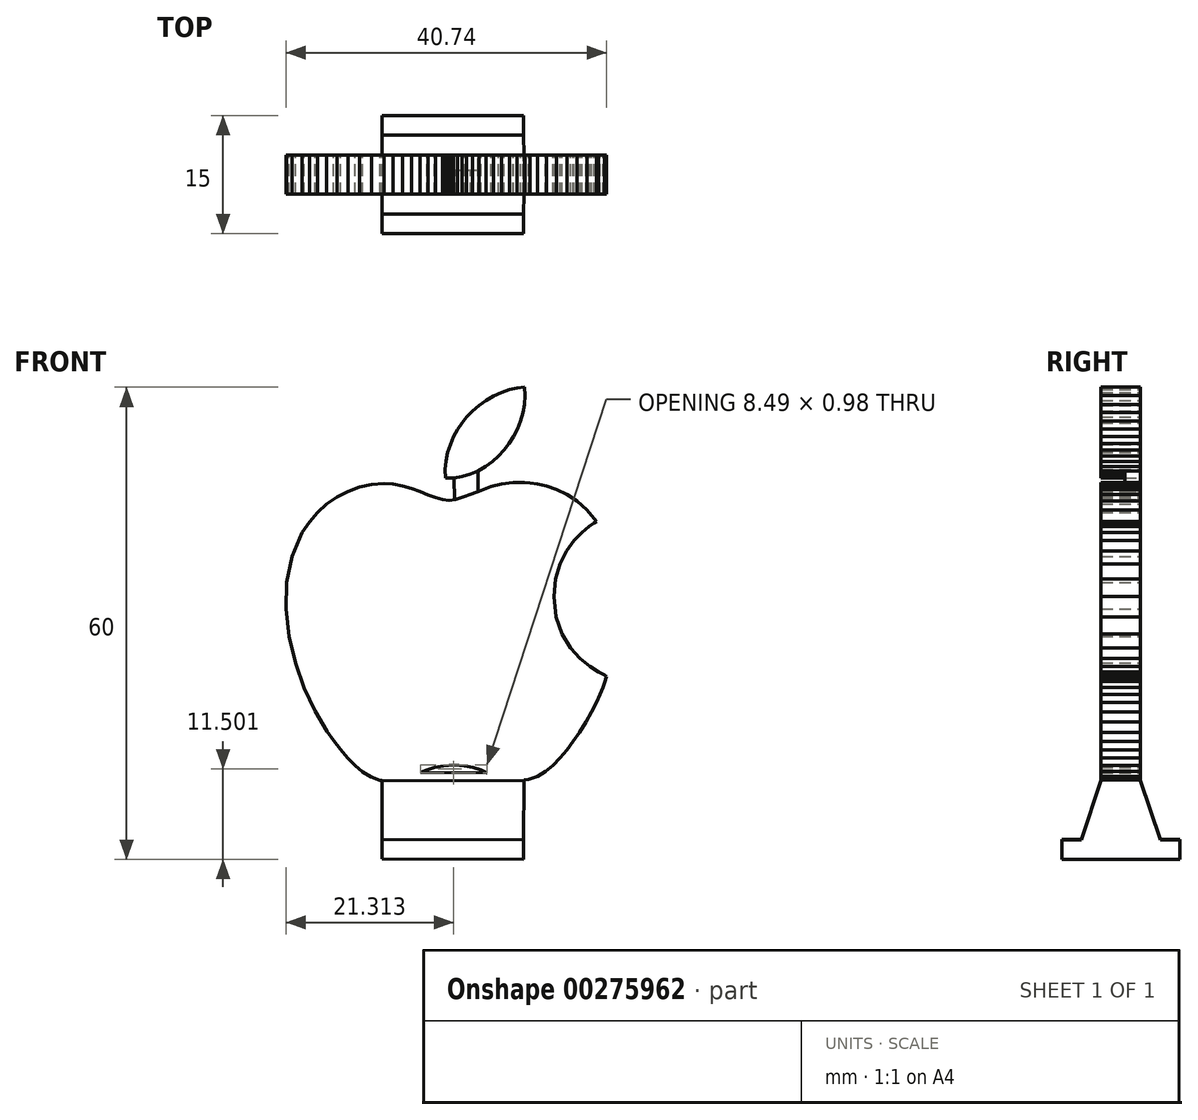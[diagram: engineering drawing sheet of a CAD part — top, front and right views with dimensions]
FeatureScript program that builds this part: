
annotation { "Feature Type Name" : "Feature", "Feature Type Description" : "" }
export const myFeature = defineFeature(function(context is Context, id is Id, definition is map)
    precondition{}
    {
        {
            var Q0;
            Q0=qCreatedBy(makeId("Front.planeOp"),FACE);
            var sketch = newSketch(context, id + "F0", { "sketchPlane" : qUnion([Q0])});
            skLineSegment(sketch, "E0", {"start": v(13.65, -1.57) * mm, "end": v(13.96, -4.18) * mm});
            skLineSegment(sketch, "E1", {"start": v(13.96, -4.18) * mm, "end": v(14.72, -6.34) * mm});
            skLineSegment(sketch, "E2", {"start": v(14.72, -6.34) * mm, "end": v(15.79, -8.1) * mm});
            skLineSegment(sketch, "E3", {"start": v(15.79, -8.1) * mm, "end": v(17, -9.46) * mm});
            skLineSegment(sketch, "E4", {"start": v(17, -9.46) * mm, "end": v(18.23, -10.48) * mm});
            skLineSegment(sketch, "E5", {"start": v(18.23, -10.48) * mm, "end": v(19.3, -11.17) * mm});
            skLineSegment(sketch, "E6", {"start": v(19.3, -11.17) * mm, "end": v(20.06, -11.56) * mm});
            skLineSegment(sketch, "E7", {"start": v(20.06, -11.56) * mm, "end": v(20.37, -11.7) * mm});
            skLineSegment(sketch, "E8", {"start": v(20.37, -11.7) * mm, "end": v(20.3, -11.9) * mm});
            skLineSegment(sketch, "E9", {"start": v(20.3, -11.9) * mm, "end": v(20.14, -12.39) * mm});
            skLineSegment(sketch, "E10", {"start": v(20.14, -12.39) * mm, "end": v(19.89, -13.1) * mm});
            skLineSegment(sketch, "E11", {"start": v(19.89, -13.1) * mm, "end": v(19.52, -14) * mm});
            skLineSegment(sketch, "E12", {"start": v(19.52, -14) * mm, "end": v(19.05, -15.06) * mm});
            skLineSegment(sketch, "E13", {"start": v(19.05, -15.06) * mm, "end": v(18.46, -16.24) * mm});
            skLineSegment(sketch, "E14", {"start": v(18.46, -16.24) * mm, "end": v(17.75, -17.5) * mm});
            skLineSegment(sketch, "E15", {"start": v(17.75, -17.5) * mm, "end": v(16.9, -18.82) * mm});
            skLineSegment(sketch, "E16", {"start": v(16.9, -18.82) * mm, "end": v(16.12, -19.95) * mm});
            skLineSegment(sketch, "E17", {"start": v(16.12, -19.95) * mm, "end": v(15.3, -21.06) * mm});
            skLineSegment(sketch, "E18", {"start": v(15.3, -21.06) * mm, "end": v(14.46, -22.09) * mm});
            skLineSegment(sketch, "E19", {"start": v(14.46, -22.09) * mm, "end": v(13.57, -23.01) * mm});
            skLineSegment(sketch, "E20", {"start": v(13.57, -23.01) * mm, "end": v(12.62, -23.8) * mm});
            skLineSegment(sketch, "E21", {"start": v(12.62, -23.8) * mm, "end": v(11.58, -24.41) * mm});
            skLineSegment(sketch, "E22", {"start": v(11.58, -24.41) * mm, "end": v(10.46, -24.81) * mm});
            skLineSegment(sketch, "E23", {"start": v(10.46, -24.81) * mm, "end": v(9.24, -24.97) * mm});
            skLineSegment(sketch, "E24", {"start": v(9.24, -24.97) * mm, "end": v(8.08, -24.9) * mm});
            skLineSegment(sketch, "E25", {"start": v(8.08, -24.9) * mm, "end": v(7.08, -24.68) * mm});
            skLineSegment(sketch, "E26", {"start": v(7.08, -24.68) * mm, "end": v(6.16, -24.37) * mm});
            skLineSegment(sketch, "E27", {"start": v(6.16, -24.37) * mm, "end": v(5.3, -24) * mm});
            skLineSegment(sketch, "E28", {"start": v(5.3, -24) * mm, "end": v(4.4, -23.63) * mm});
            skLineSegment(sketch, "E29", {"start": v(4.4, -23.63) * mm, "end": v(3.42, -23.3) * mm});
            skLineSegment(sketch, "E30", {"start": v(3.42, -23.3) * mm, "end": v(2.3, -23.07) * mm});
            skLineSegment(sketch, "E31", {"start": v(2.3, -23.07) * mm, "end": v(0.98, -22.98) * mm});
            skLineSegment(sketch, "E32", {"start": v(0.98, -22.98) * mm, "end": v(-0.34, -23.06) * mm});
            skLineSegment(sketch, "E33", {"start": v(-0.34, -23.06) * mm, "end": v(-1.47, -23.28) * mm});
            skLineSegment(sketch, "E34", {"start": v(-1.47, -23.28) * mm, "end": v(-2.46, -23.6) * mm});
            skLineSegment(sketch, "E35", {"start": v(-2.46, -23.6) * mm, "end": v(-3.37, -23.96) * mm});
            skLineSegment(sketch, "E36", {"start": v(-3.37, -23.96) * mm, "end": v(-4.24, -24.33) * mm});
            skLineSegment(sketch, "E37", {"start": v(-4.24, -24.33) * mm, "end": v(-5.14, -24.66) * mm});
            skLineSegment(sketch, "E38", {"start": v(-5.14, -24.66) * mm, "end": v(-6.12, -24.9) * mm});
            skLineSegment(sketch, "E39", {"start": v(-6.12, -24.9) * mm, "end": v(-7.22, -25.03) * mm});
            skLineSegment(sketch, "E40", {"start": v(-7.22, -25.03) * mm, "end": v(-8.42, -24.92) * mm});
            skLineSegment(sketch, "E41", {"start": v(-8.42, -24.92) * mm, "end": v(-9.55, -24.52) * mm});
            skLineSegment(sketch, "E42", {"start": v(-9.55, -24.52) * mm, "end": v(-10.62, -23.88) * mm});
            skLineSegment(sketch, "E43", {"start": v(-10.62, -23.88) * mm, "end": v(-11.62, -23.05) * mm});
            skLineSegment(sketch, "E44", {"start": v(-11.62, -23.05) * mm, "end": v(-12.57, -22.07) * mm});
            skLineSegment(sketch, "E45", {"start": v(-12.57, -22.07) * mm, "end": v(-13.47, -20.98) * mm});
            skLineSegment(sketch, "E46", {"start": v(-13.47, -20.98) * mm, "end": v(-14.32, -19.84) * mm});
            skLineSegment(sketch, "E47", {"start": v(-14.32, -19.84) * mm, "end": v(-15.13, -18.7) * mm});
            skLineSegment(sketch, "E48", {"start": v(-15.13, -18.7) * mm, "end": v(-16.68, -16.14) * mm});
            skLineSegment(sketch, "E49", {"start": v(-16.68, -16.14) * mm, "end": v(-18.06, -13.2) * mm});
            skLineSegment(sketch, "E50", {"start": v(-18.06, -13.2) * mm, "end": v(-19.19, -10) * mm});
            skLineSegment(sketch, "E51", {"start": v(-19.19, -10) * mm, "end": v(-19.98, -6.62) * mm});
            skLineSegment(sketch, "E52", {"start": v(-19.98, -6.62) * mm, "end": v(-20.37, -3.18) * mm});
            skLineSegment(sketch, "E53", {"start": v(-20.37, -3.18) * mm, "end": v(-20.27, 0.23) * mm});
            skLineSegment(sketch, "E54", {"start": v(-20.27, 0.23) * mm, "end": v(-19.6, 3.5) * mm});
            skLineSegment(sketch, "E55", {"start": v(-19.6, 3.5) * mm, "end": v(-18.3, 6.53) * mm});
            skLineSegment(sketch, "E56", {"start": v(-18.3, 6.53) * mm, "end": v(-17.4, 7.89) * mm});
            skLineSegment(sketch, "E57", {"start": v(-17.4, 7.89) * mm, "end": v(-16.36, 9.1) * mm});
            skLineSegment(sketch, "E58", {"start": v(-16.36, 9.1) * mm, "end": v(-15.18, 10.17) * mm});
            skLineSegment(sketch, "E59", {"start": v(-15.18, 10.17) * mm, "end": v(-13.9, 11.07) * mm});
            skLineSegment(sketch, "E60", {"start": v(-13.9, 11.07) * mm, "end": v(-12.51, 11.8) * mm});
            skLineSegment(sketch, "E61", {"start": v(-12.51, 11.8) * mm, "end": v(-11.05, 12.33) * mm});
            skLineSegment(sketch, "E62", {"start": v(-11.05, 12.33) * mm, "end": v(-9.52, 12.67) * mm});
            skLineSegment(sketch, "E63", {"start": v(-9.52, 12.67) * mm, "end": v(-7.94, 12.8) * mm});
            skLineSegment(sketch, "E64", {"start": v(-7.94, 12.8) * mm, "end": v(-6.74, 12.73) * mm});
            skLineSegment(sketch, "E65", {"start": v(-6.74, 12.73) * mm, "end": v(-5.57, 12.5) * mm});
            skLineSegment(sketch, "E66", {"start": v(-5.57, 12.5) * mm, "end": v(-4.43, 12.14) * mm});
            skLineSegment(sketch, "E67", {"start": v(-4.43, 12.14) * mm, "end": v(-3.34, 11.74) * mm});
            skLineSegment(sketch, "E68", {"start": v(-3.34, 11.74) * mm, "end": v(-2.31, 11.33) * mm});
            skLineSegment(sketch, "E69", {"start": v(-2.31, 11.33) * mm, "end": v(-1.35, 10.98) * mm});
            skLineSegment(sketch, "E70", {"start": v(-1.35, 10.98) * mm, "end": v(-0.47, 10.73) * mm});
            skLineSegment(sketch, "E71", {"start": v(-0.47, 10.73) * mm, "end": v(0.32, 10.63) * mm});
            skLineSegment(sketch, "E72", {"start": v(0.32, 10.63) * mm, "end": v(1.14, 10.74) * mm});
            skLineSegment(sketch, "E73", {"start": v(1.14, 10.74) * mm, "end": v(2.1, 11.04) * mm});
            skLineSegment(sketch, "E74", {"start": v(2.1, 11.04) * mm, "end": v(3.2, 11.46) * mm});
            skLineSegment(sketch, "E75", {"start": v(3.2, 11.46) * mm, "end": v(4.4, 11.93) * mm});
            skLineSegment(sketch, "E76", {"start": v(4.4, 11.93) * mm, "end": v(5.68, 12.37) * mm});
            skLineSegment(sketch, "E77", {"start": v(5.68, 12.37) * mm, "end": v(7.04, 12.73) * mm});
            skLineSegment(sketch, "E78", {"start": v(7.04, 12.73) * mm, "end": v(8.45, 12.94) * mm});
            skLineSegment(sketch, "E79", {"start": v(8.45, 12.94) * mm, "end": v(9.9, 12.93) * mm});
            skLineSegment(sketch, "E80", {"start": v(9.9, 12.93) * mm, "end": v(10.65, 12.87) * mm});
            skLineSegment(sketch, "E81", {"start": v(10.65, 12.87) * mm, "end": v(11.6, 12.73) * mm});
            skLineSegment(sketch, "E82", {"start": v(11.6, 12.73) * mm, "end": v(12.74, 12.46) * mm});
            skLineSegment(sketch, "E83", {"start": v(12.74, 12.46) * mm, "end": v(14, 12.03) * mm});
            skLineSegment(sketch, "E84", {"start": v(14, 12.03) * mm, "end": v(15.3, 11.4) * mm});
            skLineSegment(sketch, "E85", {"start": v(15.3, 11.4) * mm, "end": v(16.62, 10.54) * mm});
            skLineSegment(sketch, "E86", {"start": v(16.62, 10.54) * mm, "end": v(17.89, 9.4) * mm});
            skLineSegment(sketch, "E87", {"start": v(17.89, 9.4) * mm, "end": v(19.06, 7.96) * mm});
            skLineSegment(sketch, "E88", {"start": v(19.06, 7.96) * mm, "end": v(18.76, 7.77) * mm});
            skLineSegment(sketch, "E89", {"start": v(18.76, 7.77) * mm, "end": v(18.1, 7.3) * mm});
            skLineSegment(sketch, "E90", {"start": v(18.1, 7.3) * mm, "end": v(17.23, 6.55) * mm});
            skLineSegment(sketch, "E91", {"start": v(17.23, 6.55) * mm, "end": v(16.25, 5.52) * mm});
            skLineSegment(sketch, "E92", {"start": v(16.25, 5.52) * mm, "end": v(15.27, 4.2) * mm});
            skLineSegment(sketch, "E93", {"start": v(15.27, 4.2) * mm, "end": v(14.44, 2.57) * mm});
            skLineSegment(sketch, "E94", {"start": v(14.44, 2.57) * mm, "end": v(13.86, 0.65) * mm});
            skLineSegment(sketch, "E95", {"start": v(13.86, 0.65) * mm, "end": v(13.65, -1.57) * mm});
            skLineSegment(sketch, "E96", {"start": v(7.35, 17.04) * mm, "end": v(7.98, 17.87) * mm});
            skLineSegment(sketch, "E97", {"start": v(7.98, 17.87) * mm, "end": v(8.54, 18.77) * mm});
            skLineSegment(sketch, "E98", {"start": v(8.54, 18.77) * mm, "end": v(9.03, 19.72) * mm});
            skLineSegment(sketch, "E99", {"start": v(9.03, 19.72) * mm, "end": v(9.43, 20.73) * mm});
            skLineSegment(sketch, "E100", {"start": v(9.43, 20.73) * mm, "end": v(9.73, 21.77) * mm});
            skLineSegment(sketch, "E101", {"start": v(9.73, 21.77) * mm, "end": v(9.93, 22.84) * mm});
            skLineSegment(sketch, "E102", {"start": v(9.93, 22.84) * mm, "end": v(10, 23.93) * mm});
            skLineSegment(sketch, "E103", {"start": v(10, 23.93) * mm, "end": v(9.95, 25.03) * mm});
            skLineSegment(sketch, "E104", {"start": v(9.95, 25.03) * mm, "end": v(8.99, 24.93) * mm});
            skLineSegment(sketch, "E105", {"start": v(8.99, 24.93) * mm, "end": v(8, 24.7) * mm});
            skLineSegment(sketch, "E106", {"start": v(8, 24.7) * mm, "end": v(7, 24.34) * mm});
            skLineSegment(sketch, "E107", {"start": v(7, 24.34) * mm, "end": v(6, 23.89) * mm});
            skLineSegment(sketch, "E108", {"start": v(6, 23.89) * mm, "end": v(5.04, 23.34) * mm});
            skLineSegment(sketch, "E109", {"start": v(5.04, 23.34) * mm, "end": v(4.14, 22.7) * mm});
            skLineSegment(sketch, "E110", {"start": v(4.14, 22.7) * mm, "end": v(3.31, 22) * mm});
            skLineSegment(sketch, "E111", {"start": v(3.31, 22) * mm, "end": v(2.58, 21.24) * mm});
            skLineSegment(sketch, "E112", {"start": v(2.58, 21.24) * mm, "end": v(1.98, 20.48) * mm});
            skLineSegment(sketch, "E113", {"start": v(1.98, 20.48) * mm, "end": v(1.43, 19.64) * mm});
            skLineSegment(sketch, "E114", {"start": v(1.43, 19.64) * mm, "end": v(0.93, 18.72) * mm});
            skLineSegment(sketch, "E115", {"start": v(0.93, 18.72) * mm, "end": v(0.5, 17.74) * mm});
            skLineSegment(sketch, "E116", {"start": v(0.5, 17.74) * mm, "end": v(0.17, 16.71) * mm});
            skLineSegment(sketch, "E117", {"start": v(0.17, 16.71) * mm, "end": v(-0.05, 15.65) * mm});
            skLineSegment(sketch, "E118", {"start": v(-0.05, 15.65) * mm, "end": v(-0.14, 14.57) * mm});
            skLineSegment(sketch, "E119", {"start": v(-0.14, 14.57) * mm, "end": v(-0.08, 13.5) * mm});
            skLineSegment(sketch, "E120", {"start": v(-0.08, 13.5) * mm, "end": v(0.98, 13.5) * mm});
            skLineSegment(sketch, "E121", {"start": v(0.98, 13.5) * mm, "end": v(2.02, 13.66) * mm});
            skLineSegment(sketch, "E122", {"start": v(2.02, 13.66) * mm, "end": v(3.05, 13.96) * mm});
            skLineSegment(sketch, "E123", {"start": v(3.05, 13.96) * mm, "end": v(4.03, 14.39) * mm});
            skLineSegment(sketch, "E124", {"start": v(4.03, 14.39) * mm, "end": v(4.97, 14.93) * mm});
            skLineSegment(sketch, "E125", {"start": v(4.97, 14.93) * mm, "end": v(5.85, 15.56) * mm});
            skLineSegment(sketch, "E126", {"start": v(5.85, 15.56) * mm, "end": v(6.64, 16.27) * mm});
            skLineSegment(sketch, "E127", {"start": v(6.64, 16.27) * mm, "end": v(7.35, 17.04) * mm});
            skLineSegment(sketch, "E128", {"start": v(0.98, 13.5) * mm, "end": v(1.14, 8.27) * mm});
            skLineSegment(sketch, "E129", {"start": v(4.03, 14.39) * mm, "end": v(4.03, 8.79) * mm});
            skLineSegment(sketch, "E130", {"start": v(-8.42, -24.92) * mm, "end": v(9.85, -24.97) * mm});
            skPoint(sketch, "E130.endSnap0", {"position": v(9.85, -24.9) * mm});
            skLineSegment(sketch, "E131", {"start": v(0.72, -24.94) * mm, "end": v(0.7, -28.27) * mm});
            skSolve(sketch);
        }
        {
            var Q0;
            Q0=makeQuery(id+"F0.imprint","IMPRINT",FACE,{"disambiguationData":[TD([[makeQuery(id+"F0.imprint","IMPRINT",EDGE,{"derivedFrom":sQuery(id+"F0.wireOp",EDGE,"E0")}),-1.0]])]});
            var Q1;
            {var subQ4=sQuery(id+"F0.wireOp",EDGE,"E73");Q1=makeQuery(id+"F0.imprint","IMPRINT",FACE,{"disambiguationData":[TD([[makeQuery(id+"F0.imprint","IMPRINT",EDGE,{"derivedFrom":subQ4}),1.0]])]});}
            var Q2;
            Q2=makeQuery(id+"F0.imprint","IMPRINT",FACE,{"disambiguationData":[TD([[makeQuery(id+"F0.imprint","IMPRINT",EDGE,{"derivedFrom":sQuery(id+"F0.wireOp",EDGE,"E96")}),1.0]])]});
            extrude(context, id + "F1", {"entities" : qUnion([Q0, Q1, Q2]), "depth" : 2 * mm});
        }
        {
            var Q0;
            Q0=makeQuery(id+"F0.imprint","IMPRINT",FACE,{"disambiguationData":[TD([[makeQuery(id+"F0.imprint","IMPRINT",EDGE,{"derivedFrom":sQuery(id+"F0.wireOp",EDGE,"E0")}),-1.0]])]});
            var Q1;
            Q1=makeQuery(id+"F0.imprint","IMPRINT",FACE,{"disambiguationData":[TD([[makeQuery(id+"F0.imprint","IMPRINT",EDGE,{"derivedFrom":sQuery(id+"F0.wireOp",EDGE,"E96")}),1.0]])]});
            extrude(context, id + "F2", {"entities" : qUnion([Q0, Q1]), "operationType" : NewBodyOperationType.ADD, "depth" : 5 * mm});
        }
        {
            var Q0;
            Q0=sQuery(id+"F0.wireOp",EDGE,"E130");
            var Q1;
            Q1=sQuery(id+"F0.wireOp",VERTEX,"E130.endSnap0");
            cPlane(context, id + "F3", {"entities" : qUnion([Q0, Q1]), "cplaneType" : CPlaneType.LINE_POINT, "offset" : 25 * mm, "width" : 150 * mm, "height" : 150 * mm});
        }
        {
            var Q0;
            Q0=qCreatedBy(id+"F3.planeOp",FACE);
            var sketch = newSketch(context, id + "F4", { "sketchPlane" : qUnion([Q0])});
            skLineSegment(sketch, "E132", {"start": v(-5, -24.94) * mm, "end": v(-7.5, -32.44) * mm});
            skLineSegment(sketch, "E133", {"start": v(-7.5, -32.44) * mm, "end": v(-10, -32.44) * mm});
            skLineSegment(sketch, "E134", {"start": v(-10, -32.44) * mm, "end": v(-10, -34.94) * mm});
            skLineSegment(sketch, "E135", {"start": v(-10, -34.94) * mm, "end": v(5, -34.94) * mm});
            skLineSegment(sketch, "E136", {"start": v(5, -34.94) * mm, "end": v(5, -32.44) * mm});
            skLineSegment(sketch, "E137", {"start": v(5, -32.44) * mm, "end": v(2.5, -32.44) * mm});
            skLineSegment(sketch, "E138", {"start": v(2.5, -32.44) * mm, "end": v(0, -24.94) * mm});
            skLineSegment(sketch, "E139", {"start": v(0, -24.94) * mm, "end": v(-5, -24.94) * mm});
            skLineSegment(sketch, "E140", {"start": v(-2.5, -24.94) * mm, "end": v(-2.5, -34.94) * mm});
            skLineSegment(sketch, "E141.top", {"start": v(0, -23.94) * mm, "end": v(-5, -23.94) * mm});
            skLineSegment(sketch, "E141.left", {"start": v(0, -24.94) * mm, "end": v(0, -23.94) * mm});
            skLineSegment(sketch, "E141.right", {"start": v(-5, -24.94) * mm, "end": v(-5, -23.94) * mm});
            skSolve(sketch);
        }
        {
            var Q0;
            {var subQ1=sQuery(id+"F4.wireOp",EDGE,"E136");Q0=makeQuery(id+"F4.imprint","IMPRINT",FACE,{"disambiguationData":[TD([[makeQuery(id+"F4.imprint","IMPRINT",EDGE,{"derivedFrom":subQ1}),1.0]])]});}
            var Q1;
            {var subQ3=sQuery(id+"F4.wireOp",EDGE,"E132");Q1=makeQuery(id+"F4.imprint","IMPRINT",FACE,{"disambiguationData":[TD([[makeQuery(id+"F4.imprint","IMPRINT",EDGE,{"derivedFrom":subQ3}),1.0]])]});}
            var Q2;
            Q2=makeQuery(id+"F4.imprint","IMPRINT",FACE,{"disambiguationData":[TD([[makeQuery(id+"F4.imprint","IMPRINT",EDGE,{"derivedFrom":sQuery(id+"F4.wireOp",EDGE,"E141.top")}),1.0]])]});
            extrude(context, id + "F5", {"entities" : qUnion([Q0, Q1, Q2]), "operationType" : NewBodyOperationType.ADD, "oppositeDirection" : true, "depth" : 18 * mm});
        }
    });
